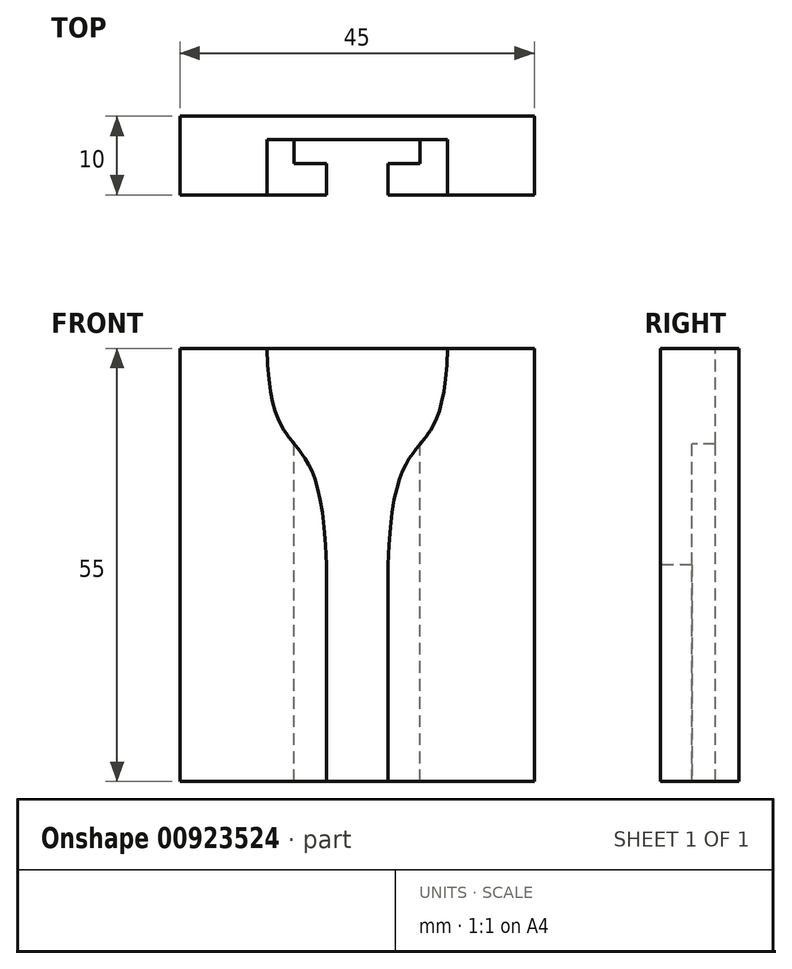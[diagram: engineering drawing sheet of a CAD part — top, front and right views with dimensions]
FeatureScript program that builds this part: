
annotation { "Feature Type Name" : "Feature", "Feature Type Description" : "" }
export const myFeature = defineFeature(function(context is Context, id is Id, definition is map)
    precondition{}
    {
        {
            var Q0;
            Q0=qCreatedBy(makeId("Front.planeOp"),FACE);
            var sketch = newSketch(context, id + "F0", { "sketchPlane" : qUnion([Q0])});
            skLineSegment(sketch, "E0.bottom", {"start": v(22.5, 27.5) * mm, "end": v(-22.5, 27.5) * mm});
            skLineSegment(sketch, "E0.top", {"start": v(22.5, -27.5) * mm, "end": v(-22.5, -27.5) * mm});
            skLineSegment(sketch, "E0.left", {"start": v(22.5, 27.5) * mm, "end": v(22.5, -27.5) * mm});
            skLineSegment(sketch, "E0.right", {"start": v(-22.5, 27.5) * mm, "end": v(-22.5, -27.5) * mm});
            skSolve(sketch);
        }
        {
            var Q0;
            Q0 = qSketchRegion(id + "F0", true);
            extrude(context, id + "F1", {"entities" : qUnion([Q0]), "depth" : 10 * mm, "offsetDistance" : 25 * mm});
        }
        {
            var Q0;
            Q0=makeQuery(id+"F1.opExtrude","CAP_FACE",FACE,{"disambiguationData":[OSD([sQuery(id+"F0.wireOp",EDGE,"E0.bottom"),sQuery(id+"F0.wireOp",EDGE,"E0.top"),sQuery(id+"F0.wireOp",EDGE,"E0.left"),sQuery(id+"F0.wireOp",EDGE,"E0.right")])],"isStart":false});
            var sketch = newSketch(context, id + "F2", { "sketchPlane" : qUnion([Q0])});
            skFitSpline(sketch, "E1", {"points": [v(3.91, 0) * mm, v(11.48, 27.5) * mm], "startDerivative": vector(1.89, 62.06) * mm, "endDerivative": vector(1.62, 51.7) * mm});
            skLineSegment(sketch, "E2", {"start": v(3.91, 0) * mm, "end": v(3.91, -27.5) * mm});
            skLineSegment(sketch, "E3", {"start": v(0, 27.5) * mm, "end": v(0, -27.5) * mm, "construction": true});
            skLineSegment(sketch, "E4.MirrorCS", {"start": v(-3.91, 0) * mm, "end": v(-3.91, -27.5) * mm});
            skFitSpline(sketch, "E5.MirrorCS", {"points": [v(-3.91, 0) * mm, v(-11.48, 27.5) * mm], "startDerivative": vector(-1.89, 62.06) * mm, "endDerivative": vector(-1.62, 51.7) * mm});
            skLineSegment(sketch, "E6", {"start": v(-11.48, 27.5) * mm, "end": v(11.48, 27.5) * mm});
            skLineSegment(sketch, "E7", {"start": v(3.91, -27.5) * mm, "end": v(0, -27.5) * mm});
            skLineSegment(sketch, "E8", {"start": v(0, -27.5) * mm, "end": v(-3.91, -27.5) * mm});
            skSolve(sketch);
        }
        {
            var Q0;
            Q0=makeQuery(id+"F2.imprint","IMPRINT",FACE,{"disambiguationData":[TD([[makeQuery(id+"F2.imprint","IMPRINT",EDGE,{"derivedFrom":sQuery(id+"F2.wireOp",EDGE,"E1")}),1.0]])]});
            extrude(context, id + "F3", {"entities" : qUnion([Q0]), "operationType" : NewBodyOperationType.REMOVE, "oppositeDirection" : true, "depth" : 7 * mm, "offsetDistance" : 25 * mm});
        }
        {
            var Q0;
            Q0=makeQuery(id+"F1.opExtrude","SWEPT_FACE",FACE,{"disambiguationData":[OSD([sQuery(id+"F0.wireOp",EDGE,"E0.bottom")])]});
            var sketch = newSketch(context, id + "F4", { "sketchPlane" : qUnion([Q0])});
            skLineSegment(sketch, "E9.bottom", {"start": v(8, -3) * mm, "end": v(-8, -3) * mm});
            skLineSegment(sketch, "E9.top", {"start": v(8, -6) * mm, "end": v(-8, -6) * mm});
            skLineSegment(sketch, "E9.left", {"start": v(8, -3) * mm, "end": v(8, -6) * mm});
            skLineSegment(sketch, "E9.right", {"start": v(-8, -3) * mm, "end": v(-8, -6) * mm});
            skPoint(sketch, "E9.middle", {"position": v(0, -4.5) * mm});
            skSolve(sketch);
        }
        {
            var Q0;
            Q0 = qSketchRegion(id + "F4", true);
            extrude(context, id + "F5", {"entities" : qUnion([Q0]), "operationType" : NewBodyOperationType.REMOVE, "endBound" : BoundingType.THROUGH_ALL, "oppositeDirection" : true, "depth" : 25 * mm, "offsetDistance" : 25 * mm});
        }
    });
